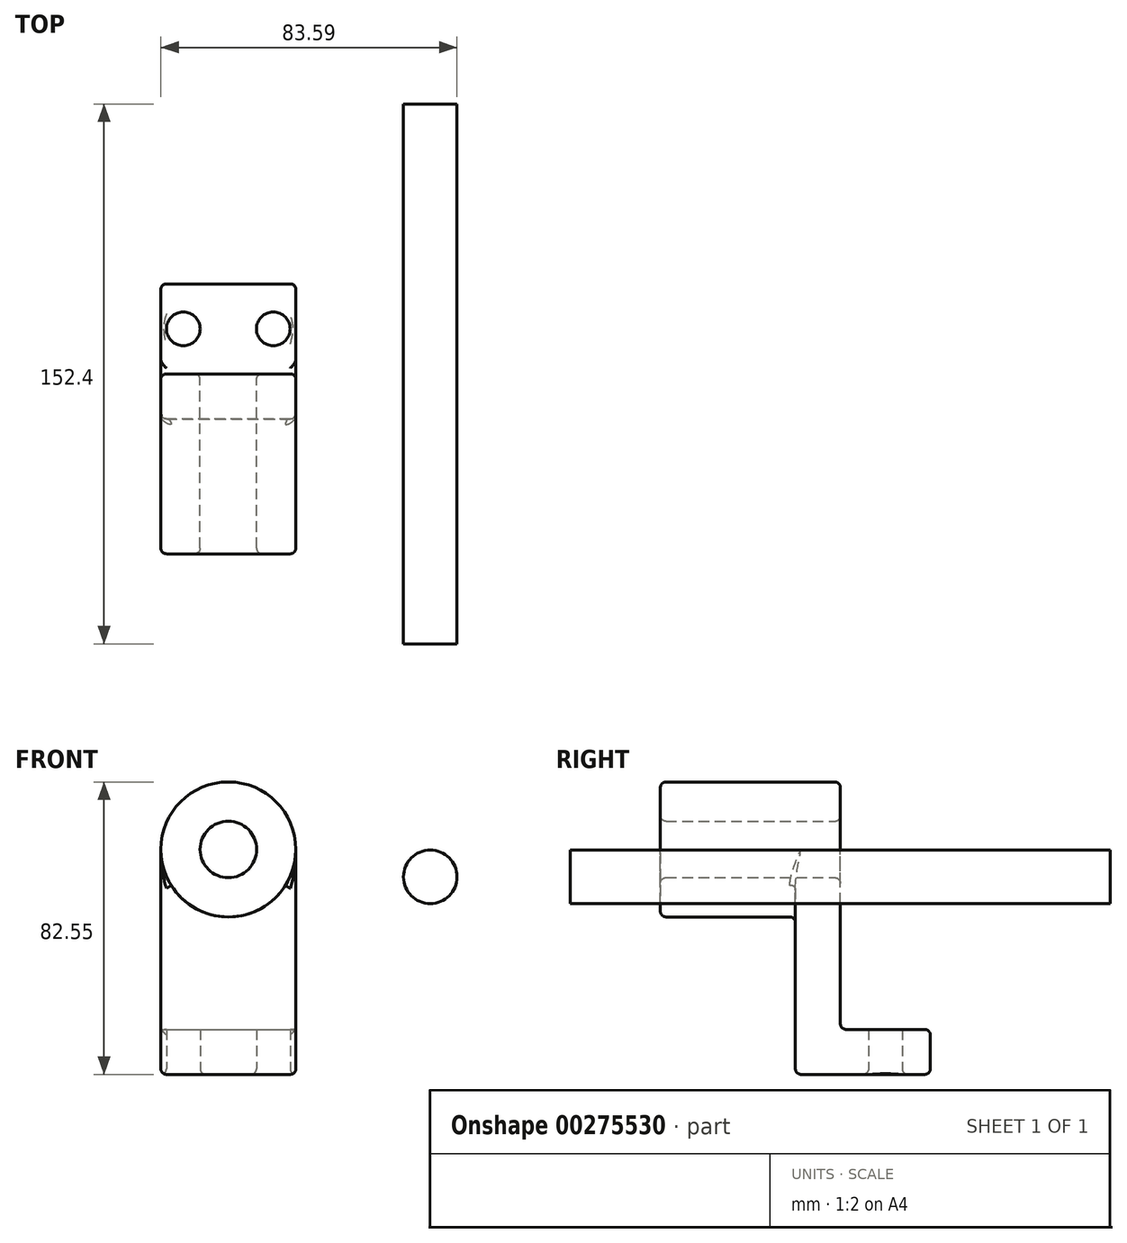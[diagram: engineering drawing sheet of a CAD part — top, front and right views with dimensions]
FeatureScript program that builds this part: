
annotation { "Feature Type Name" : "Feature", "Feature Type Description" : "" }
export const myFeature = defineFeature(function(context is Context, id is Id, definition is map)
    precondition{}
    {
        {
            var Q0;
            Q0=qCreatedBy(makeId("Front.planeOp"),FACE);
            var sketch = newSketch(context, id + "F0", { "sketchPlane" : qUnion([Q0])});
            skLineSegment(sketch, "E0.bottom", {"start": v(-21.15, -31.75) * mm, "end": v(-59.25, -31.75) * mm});
            skLineSegment(sketch, "E0.top", {"start": v(-21.15, 31.75) * mm, "end": v(-59.25, 31.75) * mm});
            skLineSegment(sketch, "E0.left", {"start": v(-21.15, -31.75) * mm, "end": v(-21.15, 31.75) * mm});
            skLineSegment(sketch, "E0.right", {"start": v(-59.25, -31.75) * mm, "end": v(-59.25, 31.75) * mm});
            skPoint(sketch, "E0.middle", {"position": v(-40.2, 0) * mm});
            skCircle(sketch, "E1", {"center": v(-40.2, 31.75) * mm, "radius": 19.05 * mm});
            skCircle(sketch, "E2", {"center": v(-40.2, 31.75) * mm, "radius": 7.97 * mm});
            skSolve(sketch);
        }
        {
            var Q0;
            {var subQ1=sQuery(id+"F0.wireOp",EDGE,"E0.top");var subQ3=sQuery(id+"F0.wireOp",EDGE,"E2");var subQ4=makeQuery(id+"F0.imprint","INTERSECT",VERTEX,{"disambiguationData":[OD(0.0)],"derivedFrom":[subQ1,subQ3]});Q0=makeQuery(id+"F0.imprint","IMPRINT",FACE,{"disambiguationData":[TD([[makeQuery(id+"F0.imprint","IMPRINT",EDGE,{"disambiguationData":[TD([[subQ4,1.0]])],"derivedFrom":subQ3}),-1.0]])]});}
            var Q1;
            {var subQ1=sQuery(id+"F0.wireOp",EDGE,"E0.top");var subQ3=sQuery(id+"F0.wireOp",EDGE,"E2");var subQ4=makeQuery(id+"F0.imprint","INTERSECT",VERTEX,{"disambiguationData":[OD(0.0)],"derivedFrom":[subQ1,subQ3]});Q1=makeQuery(id+"F0.imprint","IMPRINT",FACE,{"disambiguationData":[TD([[makeQuery(id+"F0.imprint","IMPRINT",EDGE,{"disambiguationData":[TD([[subQ4,-1.0]])],"derivedFrom":subQ3}),-1.0]])]});}
            var Q2;
            Q2=makeQuery(id+"F0.imprint","IMPRINT",FACE,{"disambiguationData":[TD([[makeQuery(id+"F0.imprint","IMPRINT",EDGE,{"derivedFrom":sQuery(id+"F0.wireOp",EDGE,"E0.bottom")}),-1.0]])]});
            extrude(context, id + "F1", {"entities" : qUnion([Q0, Q1, Q2]), "depth" : 12.7 * mm});
        }
        {
            var Q0;
            {var subQ1=sQuery(id+"F0.wireOp",EDGE,"E0.top");var subQ3=sQuery(id+"F0.wireOp",EDGE,"E2");var subQ4=makeQuery(id+"F0.imprint","INTERSECT",VERTEX,{"disambiguationData":[OD(0.0)],"derivedFrom":[subQ1,subQ3]});Q0=makeQuery(id+"F0.imprint","IMPRINT",FACE,{"disambiguationData":[TD([[makeQuery(id+"F0.imprint","IMPRINT",EDGE,{"disambiguationData":[TD([[subQ4,1.0]])],"derivedFrom":subQ3}),-1.0]])]});}
            var Q1;
            {var subQ1=sQuery(id+"F0.wireOp",EDGE,"E0.top");var subQ3=sQuery(id+"F0.wireOp",EDGE,"E2");var subQ4=makeQuery(id+"F0.imprint","INTERSECT",VERTEX,{"disambiguationData":[OD(0.0)],"derivedFrom":[subQ1,subQ3]});Q1=makeQuery(id+"F0.imprint","IMPRINT",FACE,{"disambiguationData":[TD([[makeQuery(id+"F0.imprint","IMPRINT",EDGE,{"disambiguationData":[TD([[subQ4,-1.0]])],"derivedFrom":subQ3}),-1.0]])]});}
            extrude(context, id + "F2", {"entities" : qUnion([Q0, Q1]), "operationType" : NewBodyOperationType.ADD, "depth" : 50.8 * mm});
        }
        {
            var Q0;
            Q0=makeQuery(id+"F1.opExtrude","SWEPT_FACE",FACE,{"disambiguationData":[OSD([sQuery(id+"F0.wireOp",EDGE,"E0.bottom")])]});
            var sketch = newSketch(context, id + "F3", { "sketchPlane" : qUnion([Q0])});
            skLineSegment(sketch, "E3.bottom", {"start": v(-59.25, 12.7) * mm, "end": v(-21.15, 12.7) * mm});
            skLineSegment(sketch, "E3.top", {"start": v(-59.25, -25.4) * mm, "end": v(-21.15, -25.4) * mm});
            skLineSegment(sketch, "E3.left", {"start": v(-59.25, 12.7) * mm, "end": v(-59.25, -25.4) * mm});
            skLineSegment(sketch, "E3.right", {"start": v(-21.15, 12.7) * mm, "end": v(-21.15, -25.4) * mm});
            skCircle(sketch, "E4", {"center": v(-52.9, -12.7) * mm, "radius": 4.76 * mm});
            skLineSegment(sketch, "E5", {"start": v(-40.2, 12.7) * mm, "end": v(-40.2, -25.4) * mm, "construction": true});
            skCircle(sketch, "E6.MirrorC", {"center": v(-27.5, -12.7) * mm, "radius": 4.76 * mm});
            skSolve(sketch);
        }
        {
            var Q0;
            Q0 = qSketchRegion(id + "F3", true);
            extrude(context, id + "F4", {"entities" : qUnion([Q0]), "operationType" : NewBodyOperationType.ADD, "oppositeDirection" : true, "depth" : 12.7 * mm});
        }
        {
            var Q0;
            {var subQ0=sQuery(id+"F0.wireOp",EDGE,"E1");Q0=makeQuery(id+"F2.boolean.opBoolean","INTERSECT",EDGE,{"derivedFrom":[makeQuery(id+"F1.opExtrude","CAP_FACE",FACE,{"disambiguationData":[OSD([sQuery(id+"F0.wireOp",EDGE,"E0.bottom"),sQuery(id+"F0.wireOp",EDGE,"E0.left"),sQuery(id+"F0.wireOp",EDGE,"E0.right"),subQ0,sQuery(id+"F0.wireOp",EDGE,"E2")])],"isStart":false}),makeQuery(id+"F2.opExtrude","SWEPT_FACE",FACE,{"disambiguationData":[OSD([subQ0])]})]});}
            var Q1;
            Q1=makeQuery(id+"F1.opExtrude","SWEPT_EDGE",EDGE,{"disambiguationData":[OSD([sQuery(id+"F0.wireOp",EDGE,"E0.top"),sQuery(id+"F0.wireOp",EDGE,"E0.right"),sQuery(id+"F0.wireOp",EDGE,"E1")])]});
            var Q2;
            Q2=makeQuery(id+"F1.opExtrude","CAP_EDGE",EDGE,{"disambiguationData":[OSD([sQuery(id+"F0.wireOp",EDGE,"E0.bottom")])],"isStart":false});
            var Q3;
            Q3=makeQuery(id+"F4.opExtrude","CAP_EDGE",EDGE,{"disambiguationData":[OSD([sQuery(id+"F3.wireOp",EDGE,"E4")])],"isStart":true});
            var Q4;
            Q4=makeQuery(id+"F4.opExtrude","CAP_EDGE",EDGE,{"disambiguationData":[OSD([sQuery(id+"F3.wireOp",EDGE,"E6.MirrorC")])],"isStart":true});
            var Q5;
            Q5=makeQuery(id+"F2.opExtrude","CAP_EDGE",EDGE,{"disambiguationData":[OSD([sQuery(id+"F0.wireOp",EDGE,"E1")])],"isStart":false});
            var Q6;
            Q6=makeQuery(id+"F2.opExtrude","CAP_EDGE",EDGE,{"disambiguationData":[OSD([sQuery(id+"F0.wireOp",EDGE,"E2")])],"isStart":false});
            var Q7;
            Q7=makeQuery(id+"F1.opExtrude","CAP_EDGE",EDGE,{"disambiguationData":[OSD([sQuery(id+"F0.wireOp",EDGE,"E2")])],"isStart":true});
            var Q8;
            Q8=makeQuery(id+"F1.opExtrude","CAP_FACE",FACE,{"disambiguationData":[OSD([sQuery(id+"F0.wireOp",EDGE,"E0.bottom"),sQuery(id+"F0.wireOp",EDGE,"E0.left"),sQuery(id+"F0.wireOp",EDGE,"E0.right"),sQuery(id+"F0.wireOp",EDGE,"E1"),sQuery(id+"F0.wireOp",EDGE,"E2")])],"isStart":true});
            var Q9;
            Q9=makeQuery(id+"F1.opExtrude","CAP_FACE",FACE,{"disambiguationData":[OSD([sQuery(id+"F0.wireOp",EDGE,"E0.bottom"),sQuery(id+"F0.wireOp",EDGE,"E0.left"),sQuery(id+"F0.wireOp",EDGE,"E0.right"),sQuery(id+"F0.wireOp",EDGE,"E1"),sQuery(id+"F0.wireOp",EDGE,"E2")])],"isStart":false});
            var Q10;
            Q10=makeQuery(id+"F4.boolean.opBoolean","MERGE",FACE,{"derivedFrom":[makeQuery(id+"F1.opExtrude","SWEPT_FACE",FACE,{"disambiguationData":[OSD([sQuery(id+"F0.wireOp",EDGE,"E0.bottom")])]}),makeQuery(id+"F4.opExtrude","CAP_FACE",FACE,{"disambiguationData":[OSD([sQuery(id+"F3.wireOp",EDGE,"E3.bottom"),sQuery(id+"F3.wireOp",EDGE,"E3.top"),sQuery(id+"F3.wireOp",EDGE,"E3.left"),sQuery(id+"F3.wireOp",EDGE,"E3.right"),sQuery(id+"F3.wireOp",EDGE,"E4"),sQuery(id+"F3.wireOp",EDGE,"E6.MirrorC")])],"isStart":true})]});
            fillet(context, id + "F5", {"entities" : qUnion([Q0, Q1, Q2, Q3, Q4, Q5, Q6, Q7, Q8, Q9, Q10]), "radius" : 1.59 * mm, "tangentPropagation" : true, "allowEdgeOverflow" : false});
        }
        {
            var Q0;
            Q0=makeQuery(id+"F4.opExtrude","SWEPT_FACE",FACE,{"disambiguationData":[OSD([sQuery(id+"F3.wireOp",EDGE,"E3.top")])]});
            fillet(context, id + "F6", {"entities" : qUnion([Q0]), "radius" : 1.59 * mm, "tangentPropagation" : true, "allowEdgeOverflow" : false});
        }
        {
            var Q0;
            Q0=qCreatedBy(makeId("Front.planeOp"),FACE);
            var sketch = newSketch(context, id + "F7", { "sketchPlane" : qUnion([Q0])});
            skCircle(sketch, "E7", {"center": v(16.78, 24) * mm, "radius": 7.56 * mm});
            skSolve(sketch);
        }
        {
            var Q0;
            Q0=makeQuery(id+"F7.imprint","IMPRINT",FACE,{"disambiguationData":[TD([[makeQuery(id+"F7.imprint","IMPRINT",EDGE,{"derivedFrom":sQuery(id+"F7.wireOp",EDGE,"E7")}),1.0]])]});
            extrude(context, id + "F8", {"entities" : qUnion([Q0]), "endBound" : BoundingType.SYMMETRIC, "depth" : 152.4 * mm});
        }
    });
